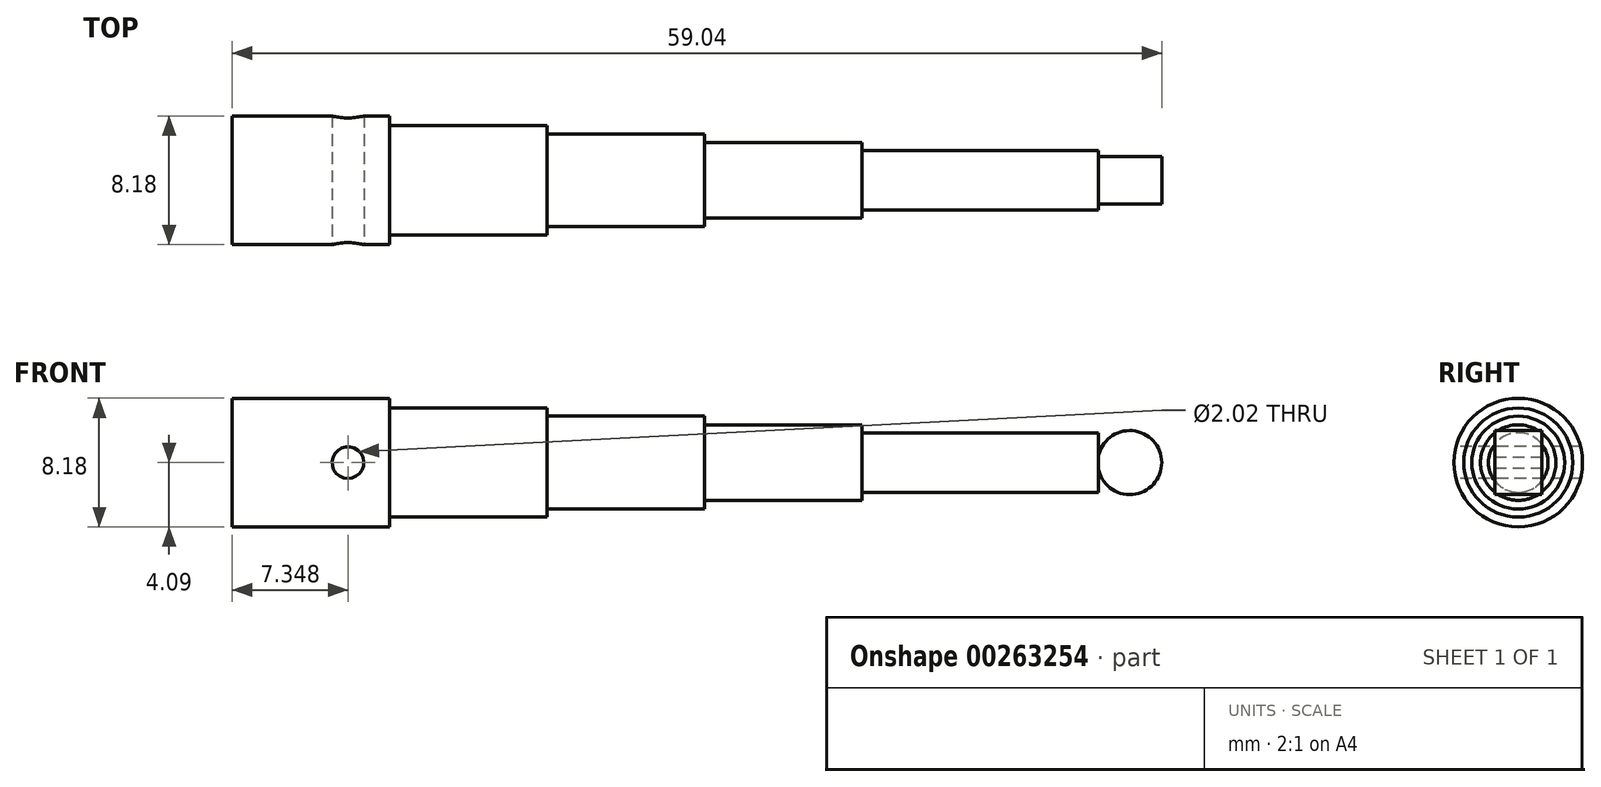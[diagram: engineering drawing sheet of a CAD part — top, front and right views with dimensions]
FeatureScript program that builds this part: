
annotation { "Feature Type Name" : "Feature", "Feature Type Description" : "" }
export const myFeature = defineFeature(function(context is Context, id is Id, definition is map)
    precondition{}
    {
        {
            var Q0;
            Q0=qCreatedBy(makeId("Right.planeOp"),FACE);
            var sketch = newSketch(context, id + "F0", { "sketchPlane" : qUnion([Q0])});
            skCircle(sketch, "E0", {"center": v(0, 0) * mm, "radius": 4.09 * mm});
            skSolve(sketch);
        }
        {
            var Q0;
            Q0 = qSketchRegion(id + "F0", true);
            extrude(context, id + "F1", {"entities" : qUnion([Q0]), "depth" : 10 * mm});
        }
        {
            var Q0;
            Q0=makeQuery(id+"F1.opExtrude","CAP_FACE",FACE,{"disambiguationData":[OSD([sQuery(id+"F0.wireOp",EDGE,"E0")])],"isStart":false});
            var sketch = newSketch(context, id + "F2", { "sketchPlane" : qUnion([Q0])});
            skCircle(sketch, "E1", {"center": v(0, 0) * mm, "radius": 3.46 * mm});
            skSolve(sketch);
        }
        {
            var Q0;
            Q0 = qSketchRegion(id + "F2", true);
            extrude(context, id + "F3", {"entities" : qUnion([Q0]), "operationType" : NewBodyOperationType.ADD, "depth" : 10 * mm});
        }
        {
            var Q0;
            Q0=makeQuery(id+"F3.opExtrude","CAP_FACE",FACE,{"disambiguationData":[OSD([sQuery(id+"F2.wireOp",EDGE,"E1")])],"isStart":false});
            var sketch = newSketch(context, id + "F4", { "sketchPlane" : qUnion([Q0])});
            skCircle(sketch, "E2", {"center": v(0, 0) * mm, "radius": 2.95 * mm});
            skSolve(sketch);
        }
        {
            var Q0;
            Q0 = qSketchRegion(id + "F4", true);
            extrude(context, id + "F5", {"entities" : qUnion([Q0]), "operationType" : NewBodyOperationType.ADD, "depth" : 10 * mm});
        }
        {
            var Q0;
            Q0=makeQuery(id+"F5.opExtrude","CAP_FACE",FACE,{"disambiguationData":[OSD([sQuery(id+"F4.wireOp",EDGE,"E2")])],"isStart":false});
            var sketch = newSketch(context, id + "F6", { "sketchPlane" : qUnion([Q0])});
            skCircle(sketch, "E3", {"center": v(0, 0) * mm, "radius": 2.4 * mm});
            skSolve(sketch);
        }
        {
            var Q0;
            Q0 = qSketchRegion(id + "F6", true);
            extrude(context, id + "F7", {"entities" : qUnion([Q0]), "operationType" : NewBodyOperationType.ADD, "depth" : 10 * mm});
        }
        {
            var Q0;
            Q0=makeQuery(id+"F7.opExtrude","CAP_FACE",FACE,{"disambiguationData":[OSD([sQuery(id+"F6.wireOp",EDGE,"E3")])],"isStart":false});
            var sketch = newSketch(context, id + "F8", { "sketchPlane" : qUnion([Q0])});
            skCircle(sketch, "E4", {"center": v(0, 0) * mm, "radius": 1.9 * mm});
            skSolve(sketch);
        }
        {
            var Q0;
            Q0 = qSketchRegion(id + "F8", true);
            extrude(context, id + "F9", {"entities" : qUnion([Q0]), "operationType" : NewBodyOperationType.ADD, "depth" : 15 * mm});
        }
        {
            var Q0;
            Q0=qCreatedBy(makeId("Front.planeOp"),FACE);
            var sketch = newSketch(context, id + "F10", { "sketchPlane" : qUnion([Q0])});
            skCircle(sketch, "E5", {"center": v(57, 0) * mm, "radius": 2.03 * mm});
            skSolve(sketch);
        }
        {
            var Q0;
            Q0 = qSketchRegion(id + "F10", true);
            extrude(context, id + "F11", {"entities" : qUnion([Q0]), "operationType" : NewBodyOperationType.ADD, "endBound" : BoundingType.SYMMETRIC, "depth" : 3 * mm});
        }
        {
            var Q0;
            Q0=qCreatedBy(makeId("Front.planeOp"),FACE);
            var sketch = newSketch(context, id + "F12", { "sketchPlane" : qUnion([Q0])});
            skArc(sketch, "E6", {"start": v(7.35, -1.01) * mm, "mid": v(8.36, 0) * mm, "end": v(7.35, 1.01) * mm});
            skArc(sketch, "E7", {"start": v(7.35, 1.01) * mm, "mid": v(6.34, 0) * mm, "end": v(7.35, -1.01) * mm});
            skSolve(sketch);
        }
        {
            var Q0;
            Q0 = qSketchRegion(id + "F12", true);
            extrude(context, id + "F13", {"entities" : qUnion([Q0]), "operationType" : NewBodyOperationType.REMOVE, "endBound" : BoundingType.SYMMETRIC, "oppositeDirection" : true, "depth" : 25 * mm});
        }
    });
